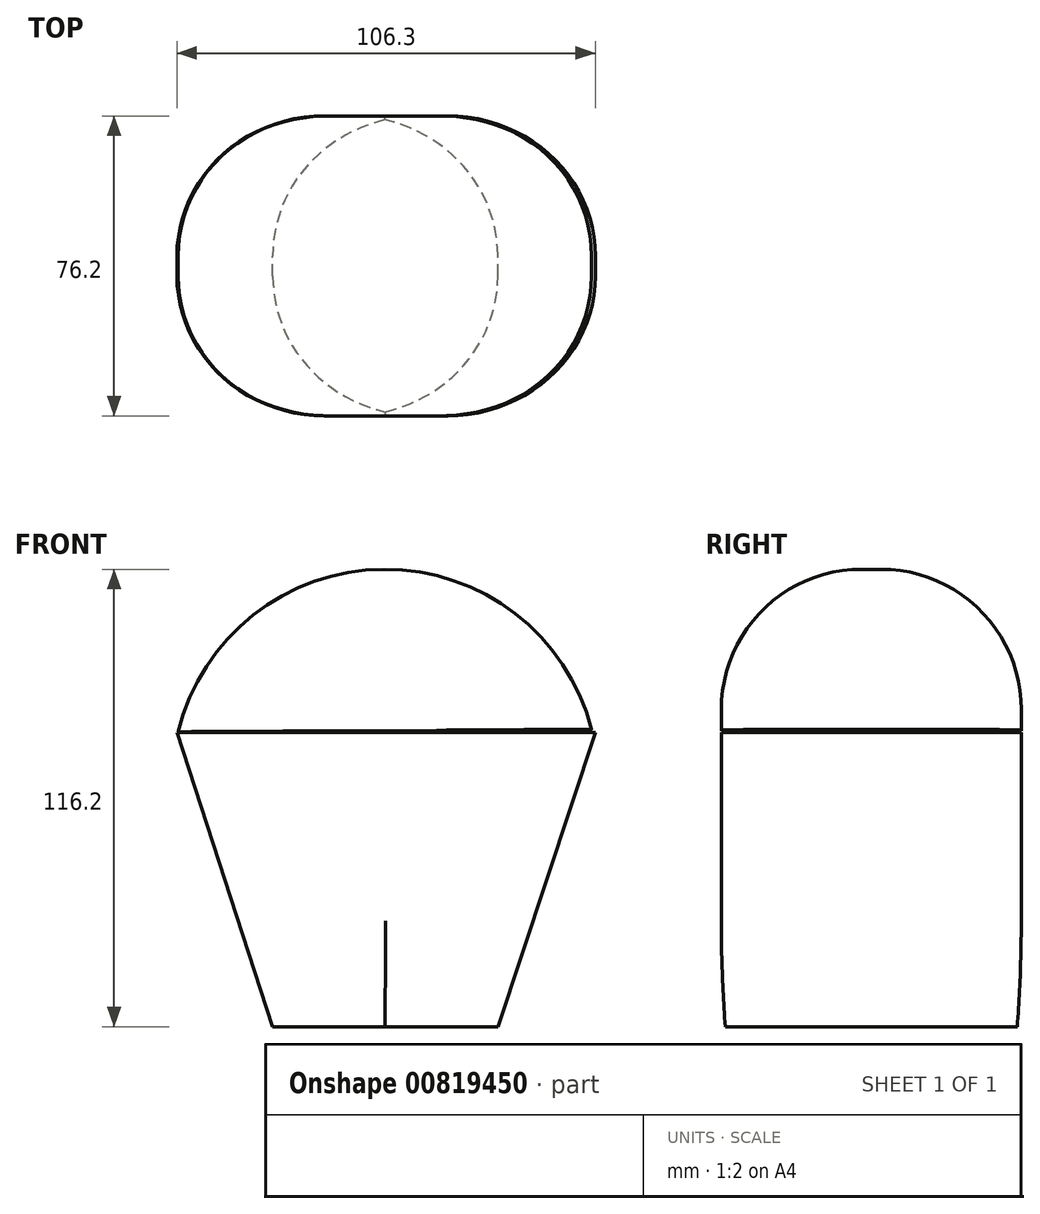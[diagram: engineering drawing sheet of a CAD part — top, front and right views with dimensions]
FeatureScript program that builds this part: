
annotation { "Feature Type Name" : "Feature", "Feature Type Description" : "" }
export const myFeature = defineFeature(function(context is Context, id is Id, definition is map)
    precondition{}
    {
        {
            var Q0;
            Q0=qCreatedBy(makeId("Front.planeOp"),FACE);
            var sketch = newSketch(context, id + "F0", { "sketchPlane" : qUnion([Q0])});
            skLineSegment(sketch, "E0.top", {"start": v(53.15, 37.38) * mm, "end": v(-53.15, 37.38) * mm});
            skPoint(sketch, "E0.middle", {"position": v(0, 0) * mm});
            skLineSegment(sketch, "E1", {"start": v(-53.15, 37.38) * mm, "end": v(-28.81, -37.38) * mm});
            skLineSegment(sketch, "E2", {"start": v(53.15, 37.38) * mm, "end": v(28.36, -37.38) * mm});
            skLineSegment(sketch, "E3", {"start": v(-28.81, -37.38) * mm, "end": v(28.36, -37.38) * mm});
            skSolve(sketch);
        }
        {
            var Q0;
            Q0=makeQuery(id+"F0.imprint","IMPRINT",FACE,{"disambiguationData":[TD([[makeQuery(id+"F0.imprint","IMPRINT",EDGE,{"derivedFrom":sQuery(id+"F0.wireOp",EDGE,"E0.top")}),1.0]])]});
            extrude(context, id + "F1", {"entities" : qUnion([Q0]), "depth" : 76.2 * mm, "offsetDistance" : 25.4 * mm});
        }
        {
            var Q0;
            Q0=makeQuery(id+"F1.opExtrude","CAP_EDGE",EDGE,{"disambiguationData":[OSD([sQuery(id+"F0.wireOp",EDGE,"E2")])],"isStart":false});
            var Q1;
            Q1=makeQuery(id+"F1.opExtrude","CAP_EDGE",EDGE,{"disambiguationData":[OSD([sQuery(id+"F0.wireOp",EDGE,"E2")])],"isStart":true});
            var Q2;
            Q2=makeQuery(id+"F1.opExtrude","CAP_EDGE",EDGE,{"disambiguationData":[OSD([sQuery(id+"F0.wireOp",EDGE,"E1")])],"isStart":false});
            var Q3;
            Q3=makeQuery(id+"F1.opExtrude","CAP_EDGE",EDGE,{"disambiguationData":[OSD([sQuery(id+"F0.wireOp",EDGE,"E1")])],"isStart":true});
            fillet(context, id + "F2", {"entities" : qUnion([Q0, Q1, Q2, Q3]), "radius" : 35.56 * mm, "tangentPropagation" : true, "allowEdgeOverflow" : false});
        }
        {
            var Q0;
            Q0=qCreatedBy(makeId("Front.planeOp"),FACE);
            var sketch = newSketch(context, id + "F3", { "sketchPlane" : qUnion([Q0])});
            skArc(sketch, "E4", {"start": v(52.17, 38.18) * mm, "mid": v(-0.58, 78.82) * mm, "end": v(-52.84, 37.54) * mm});
            skLineSegment(sketch, "E5", {"start": v(-52.84, 37.54) * mm, "end": v(52.17, 38.18) * mm});
            skSolve(sketch);
        }
        {
            var Q0;
            Q0=makeQuery(id+"F3.imprint","IMPRINT",FACE,{"disambiguationData":[TD([[makeQuery(id+"F3.imprint","IMPRINT",EDGE,{"derivedFrom":sQuery(id+"F3.wireOp",EDGE,"E4")}),1.0]])]});
            extrude(context, id + "F4", {"entities" : qUnion([Q0]), "depth" : 76.2 * mm, "offsetDistance" : 25.4 * mm});
        }
        {
            var Q0;
            Q0=makeQuery(id+"F4.opExtrude","CAP_EDGE",EDGE,{"disambiguationData":[OSD([sQuery(id+"F3.wireOp",EDGE,"E4")])],"isStart":false});
            var Q1;
            Q1=makeQuery(id+"F4.opExtrude","CAP_EDGE",EDGE,{"disambiguationData":[OSD([sQuery(id+"F3.wireOp",EDGE,"E4")])],"isStart":true});
            fillet(context, id + "F5", {"entities" : qUnion([Q0, Q1]), "radius" : 35.56 * mm, "tangentPropagation" : true, "allowEdgeOverflow" : false});
        }
    });
